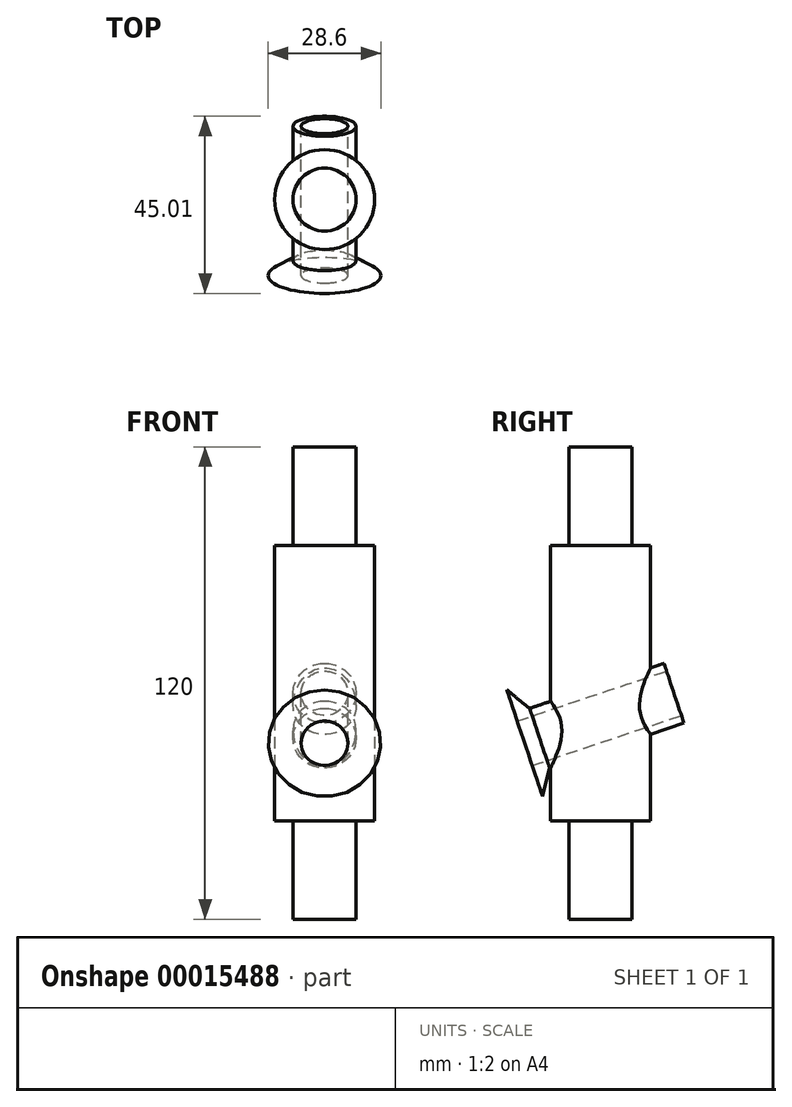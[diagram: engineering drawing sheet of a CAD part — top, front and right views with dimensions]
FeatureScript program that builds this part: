
annotation { "Feature Type Name" : "Feature", "Feature Type Description" : "" }
export const myFeature = defineFeature(function(context is Context, id is Id, definition is map)
    precondition{}
    {
        {
            var Q0;
            Q0=qCreatedBy(makeId("Top.planeOp"),FACE);
            var sketch = newSketch(context, id + "F0", { "sketchPlane" : qUnion([Q0])});
            skCircle(sketch, "E0", {"center": v(0, 0) * mm, "radius": 12.7 * mm});
            skSolve(sketch);
        }
        {
            var Q0;
            Q0=makeQuery(id+"F0.imprint","IMPRINT",FACE,{"disambiguationData":[TD([[makeQuery(id+"F0.imprint","IMPRINT",EDGE,{"derivedFrom":sQuery(id+"F0.wireOp",EDGE,"E0")}),1.0]])]});
            extrude(context, id + "F1", {"entities" : qUnion([Q0]), "depth" : 70 * mm});
        }
        {
            var Q0;
            Q0=qCreatedBy(makeId("Right.planeOp"),FACE);
            var sketch = newSketch(context, id + "F2", { "sketchPlane" : qUnion([Q0])});
            skLineSegment(sketch, "E1", {"start": v(30.21, 36.28) * mm, "end": v(-31.3, 15.7) * mm});
            skLineSegment(sketch, "E2", {"start": v(-17.41, 14.07) * mm, "end": v(-14.76, 6.16) * mm});
            skLineSegment(sketch, "E3", {"start": v(-14.76, 6.16) * mm, "end": v(-12.97, 13.4) * mm});
            skLineSegment(sketch, "E4", {"start": v(-12.97, 13.4) * mm, "end": v(21.17, 24.82) * mm});
            skLineSegment(sketch, "E5", {"start": v(21.17, 24.82) * mm, "end": v(20.52, 26.77) * mm});
            skLineSegment(sketch, "E6", {"start": v(20.52, 26.77) * mm, "end": v(-17.41, 14.07) * mm});
            skSolve(sketch);
        }
        {
            var Q0;
            Q0 = qSketchRegion(id + "F2", true);
            var Q1;
            Q1=sQuery(id+"F2.wireOp",EDGE,"E1");
            revolve(context, id + "F3", {"operationType" : NewBodyOperationType.ADD, "entities" : qUnion([Q0]), "axis" : qUnion([Q1]), "revolveType" : RevolveType.FULL});
        }
        {
            var Q0;
            Q0=makeQuery(id+"F3.opRevolve","SWEPT_FACE",FACE,{"disambiguationData":[OSD([sQuery(id+"F2.wireOp",EDGE,"E2")])]});
            var sketch = newSketch(context, id + "F4", { "sketchPlane" : qUnion([Q0])});
            skCircle(sketch, "E7", {"center": v(0, 24.82) * mm, "radius": 5.95 * mm});
            skSolve(sketch);
        }
        {
            var Q0;
            Q0 = qSketchRegion(id + "F4", true);
            extrude(context, id + "F5", {"entities" : qUnion([Q0]), "operationType" : NewBodyOperationType.REMOVE, "oppositeDirection" : true, "depth" : 49.98 * mm});
        }
        {
            var Q0;
            Q0=makeQuery(id+"F1.opExtrude","CAP_FACE",FACE,{"disambiguationData":[OSD([sQuery(id+"F0.wireOp",EDGE,"E0")])],"isStart":false});
            var sketch = newSketch(context, id + "F6", { "sketchPlane" : qUnion([Q0])});
            skCircle(sketch, "E8", {"center": v(0, 0) * mm, "radius": 8 * mm});
            skSolve(sketch);
        }
        {
            var Q0;
            Q0 = qSketchRegion(id + "F6", true);
            extrude(context, id + "F7", {"entities" : qUnion([Q0]), "operationType" : NewBodyOperationType.ADD, "depth" : 25 * mm});
        }
        {
            var Q0;
            Q0=makeQuery(id+"F1.opExtrude","CAP_FACE",FACE,{"disambiguationData":[OSD([sQuery(id+"F0.wireOp",EDGE,"E0")])],"isStart":true});
            var sketch = newSketch(context, id + "F8", { "sketchPlane" : qUnion([Q0])});
            skCircle(sketch, "E9", {"center": v(0, 0) * mm, "radius": 8 * mm});
            skSolve(sketch);
        }
        {
            var Q0;
            Q0 = qSketchRegion(id + "F8", true);
            extrude(context, id + "F9", {"entities" : qUnion([Q0]), "operationType" : NewBodyOperationType.ADD, "depth" : 25 * mm});
        }
    });
